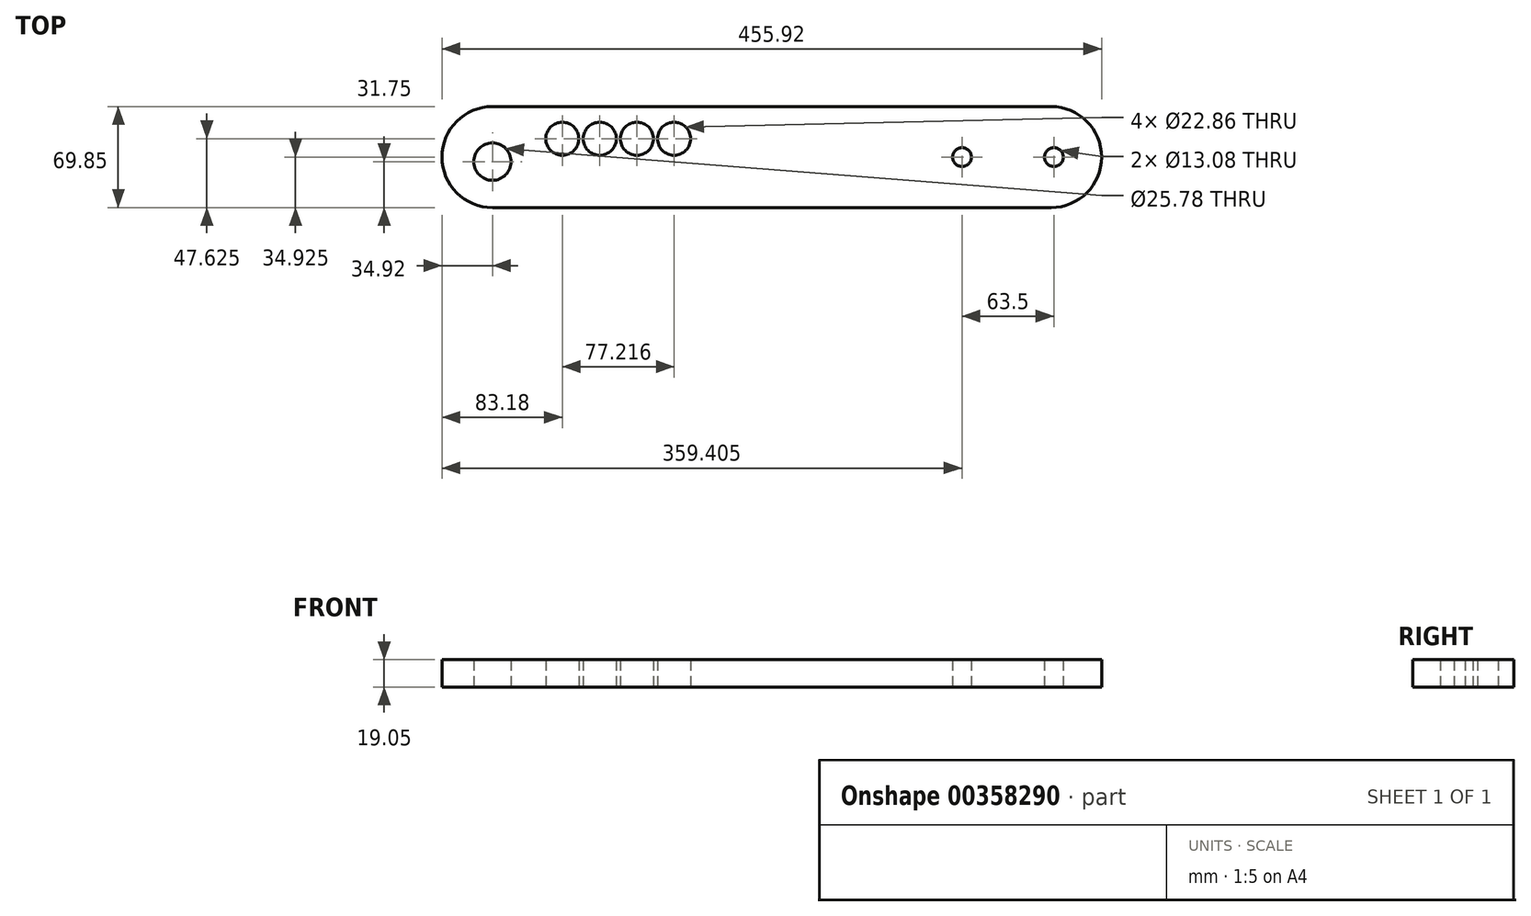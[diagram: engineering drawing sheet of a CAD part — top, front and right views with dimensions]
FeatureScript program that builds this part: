
annotation { "Feature Type Name" : "Feature", "Feature Type Description" : "" }
export const myFeature = defineFeature(function(context is Context, id is Id, definition is map)
    precondition{}
    {
        {
            var Q0;
            Q0=qCreatedBy(makeId("Top.planeOp"),FACE);
            var sketch = newSketch(context, id + "F0", { "sketchPlane" : qUnion([Q0])});
            skCircle(sketch, "E0", {"center": v(0, 0) * mm, "radius": 12.9 * mm});
            skCircle(sketch, "E1", {"center": v(48.26, 15.88) * mm, "radius": 11.43 * mm});
            skCircle(sketch, "E2", {"center": v(74.17, 15.88) * mm, "radius": 11.43 * mm});
            skCircle(sketch, "E3", {"center": v(125.48, 15.88) * mm, "radius": 11.43 * mm});
            skCircle(sketch, "E4", {"center": v(99.82, 15.88) * mm, "radius": 11.43 * mm});
            skCircle(sketch, "E5", {"center": v(324.49, 3.17) * mm, "radius": 6.54 * mm});
            skCircle(sketch, "E6", {"center": v(387.99, 3.18) * mm, "radius": 6.54 * mm});
            skLineSegment(sketch, "E7.bottom", {"start": v(0, 38.1) * mm, "end": v(421, 38.1) * mm});
            skLineSegment(sketch, "E7.top", {"start": v(0, -31.75) * mm, "end": v(421, -31.75) * mm});
            skLineSegment(sketch, "E7.right", {"start": v(421, 38.1) * mm, "end": v(421, -31.75) * mm});
            skLineSegment(sketch, "E8", {"start": v(0, 38.1) * mm, "end": v(0, 3.17) * mm, "construction": true});
            skArc(sketch, "E9", {"start": v(0, 38.1) * mm, "mid": v(-34.93, 3.18) * mm, "end": v(0, -31.75) * mm});
            skLineSegment(sketch, "E10", {"start": v(387.99, 3.18) * mm, "end": v(324.49, 3.17) * mm, "construction": true});
            skSolve(sketch);
        }
        {
            var Q0;
            Q0 = qSketchRegion(id + "F0", true);
            extrude(context, id + "F1", {"entities" : qUnion([Q0]), "depth" : 19.05 * mm});
        }
        {
            var Q0;
            Q0=makeQuery(id+"F1.opExtrude","SWEPT_EDGE",EDGE,{"disambiguationData":[OSD([sQuery(id+"F0.wireOp",EDGE,"E7.bottom"),sQuery(id+"F0.wireOp",EDGE,"E7.right")])]});
            var Q1;
            Q1=makeQuery(id+"F1.opExtrude","SWEPT_EDGE",EDGE,{"disambiguationData":[OSD([sQuery(id+"F0.wireOp",EDGE,"E7.top"),sQuery(id+"F0.wireOp",EDGE,"E7.right")])]});
            fillet(context, id + "F2", {"entities" : qUnion([Q0, Q1]), "radius" : 34.92 * mm, "tangentPropagation" : true, "allowEdgeOverflow" : false});
        }
    });
